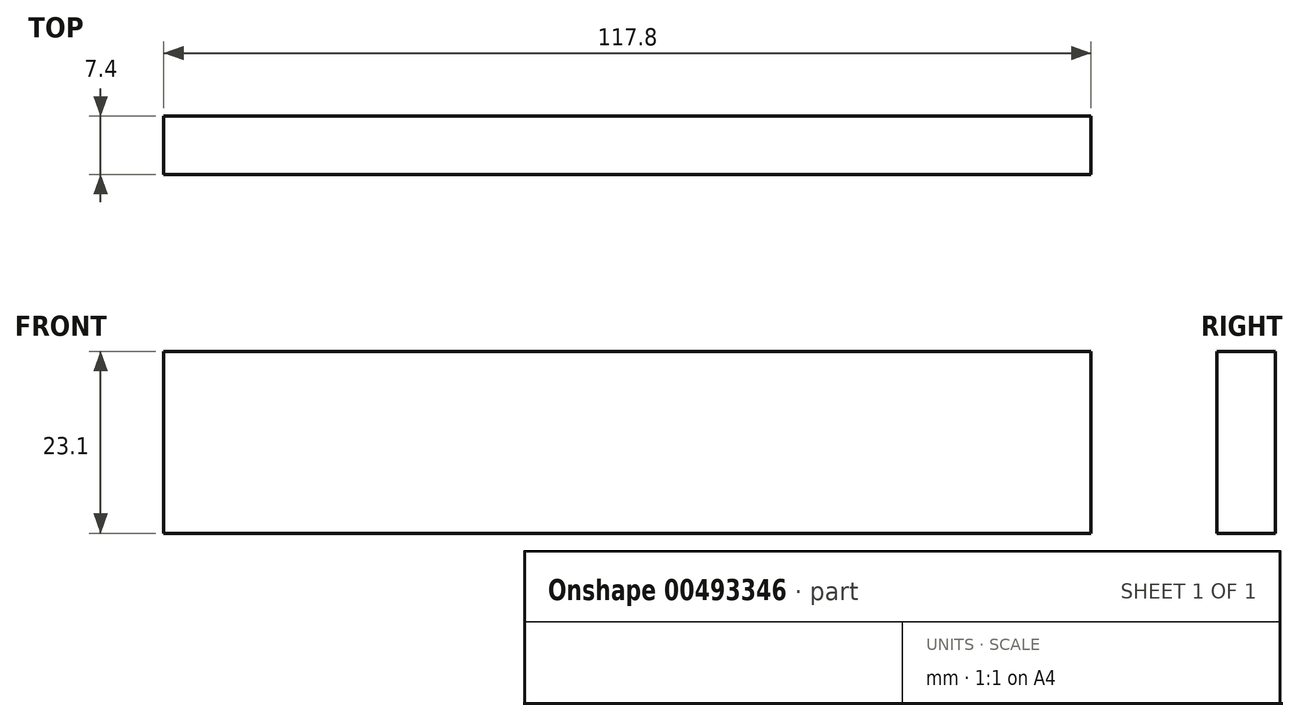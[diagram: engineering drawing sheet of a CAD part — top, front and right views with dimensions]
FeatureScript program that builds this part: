
annotation { "Feature Type Name" : "Feature", "Feature Type Description" : "" }
export const myFeature = defineFeature(function(context is Context, id is Id, definition is map)
    precondition{}
    {
        {
            var Q0;
            Q0=qCreatedBy(makeId("Front.planeOp"),FACE);
            var sketch = newSketch(context, id + "F0", { "sketchPlane" : qUnion([Q0])});
            skLineSegment(sketch, "E0.bottom", {"start": v(-58.9, 11.55) * mm, "end": v(58.9, 11.55) * mm});
            skLineSegment(sketch, "E0.top", {"start": v(-58.9, -11.55) * mm, "end": v(58.9, -11.55) * mm});
            skLineSegment(sketch, "E0.left", {"start": v(-58.9, 11.55) * mm, "end": v(-58.9, -11.55) * mm});
            skLineSegment(sketch, "E0.right", {"start": v(58.9, 11.55) * mm, "end": v(58.9, -11.55) * mm});
            skPoint(sketch, "E0.middle", {"position": v(0, 0) * mm});
            skSolve(sketch);
        }
        {
            var Q0;
            Q0 = qSketchRegion(id + "F0", true);
            extrude(context, id + "F1", {"entities" : qUnion([Q0]), "depth" : 7.4 * mm});
        }
    });
